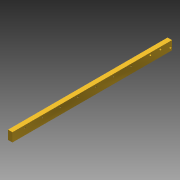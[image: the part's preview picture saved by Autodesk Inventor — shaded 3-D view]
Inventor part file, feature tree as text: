
AUTODESK INVENTOR PART (.ipt)
format: ipt  version: 2016 (Build 200138000, 138)  size: 139,264 bytes
history: native  units: in
note: dims shown in document units (in); Inventor stores cm internally (conversion verified against a paired STEP export)
features: hole x4, pattern_linear x4, sketch x3, extrude x1
ambient origin geometry x8: Origin, YZ Plane, XZ Plane, XY Plane, X Axis, Y Axis, Z Axis, Center Point
bodies: Solid1 (feature_tree)
feature tree (12):
  extrude  "Extrusion1"  Depth=0.5in
  sketch  "Sketch3"  dims[d6=9.0in d7=0.0in d8=0.1344in]
  hole  "Hole1"  [1 undecoded]
  pattern_linear  "Rectangular Pattern1"  Count1=7 Spacing1=1.0in
  sketch  "Sketch6"  dims[d9=0.7in d10=0.067in d11=0.75in d12=0.375in d13=0.25in d14=0.5635in d15=1.0in d16=0.8108in d17=2.7559in d19=1.0in d20=0.75in d23=0.8108in d24=0.5635in d25=0.25in d26=0.375in d27=0.25in d28=0.067in d45=7.793in d46=0.121in d47=0.109in d48=0.75in d49=0.375in d50=0.25in d51=0.5635in d52=0.26in d53=0.8108in d54=1.1811in d56=0.561in d57=0.7874in d59=0.197in d61=0.067in d62=0.75in d63=0.375in d64=0.25in d65=0.5635in d66=0.25in d67=0.8108in d68=2.3in d69=0.15in d70=0.7874in d72=1.0in d73=1.9685in d75=1.5in d76=0.125in d77=0.125in]
  hole  "Hole4"  [1 undecoded]
  pattern_linear  "Rectangular Pattern4"  Spacing1=7.793in  [1 undecoded]
  hole  "Hole5"  [1 undecoded]
  pattern_linear  "Rectangular Pattern5"  Count1=3 Spacing1=0.561in
  pattern_linear  "Rectangular Pattern6"  Spacing1=2.3in  [1 undecoded]
  sketch  "Sketch2"  dims[d3=0.25in d5=0.5in]
  hole  "Hole2"  [1 undecoded]
note: 6 required parameter values undecoded (feature->parameter linkage not recoverable at this tier; creation-order binding heuristic only, values carry confidence <= 0.55)
